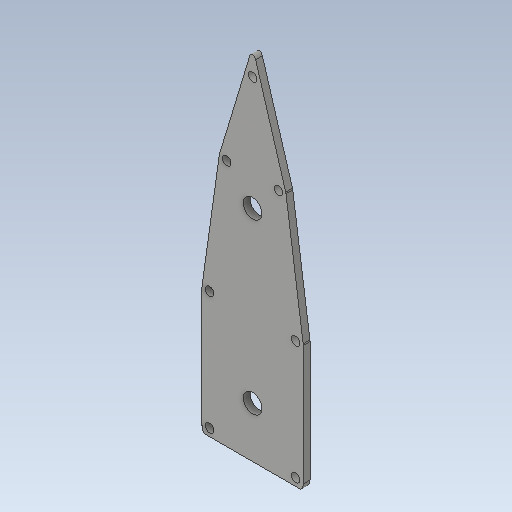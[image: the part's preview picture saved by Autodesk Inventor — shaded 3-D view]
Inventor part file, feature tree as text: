
AUTODESK INVENTOR PART (.ipt)
format: ipt  version: 2020.1 (Build 241239000, 239)  size: 233,984 bytes
history: native  units: mm
features: other x8, sketch x2, plane x1, sheet_metal_op x1, reference x1, projected_geometry x1
ambient origin geometry x8: Origin, YZ Plane, XZ Plane, XY Plane, X Axis, Y Axis, Z Axis, Center Point
bodies: Solid1 (feature_tree)
feature tree (14):
  plane  "Work Plane1"
  sheet_metal_op  "Face1"
  sketch  "Sketch1"  dims[d0=8.0mm]
  reference  "Reference1"
  other  "Plate1"
  sketch  "Sketch2"  dims[d1=22.0mm d2=22.0mm d3=10.0mm d4=10.0mm d5=10.0mm d6=10.0mm d7=10.0mm d8=10.0mm d9=10.0mm d10=10.0mm d11=10.0mm d12=10.0mm d13=10.0mm d14=10.0mm d15=9.0mm d16=9.0mm d17=4.0mm d18=9.0mm d19=9.0mm d20=9.0mm d21=9.0mm d22=9.0mm d23=9.0mm d24=9.0mm d25=9.0mm d26=9.0mm d27=9.0mm d28=9.0mm d29=9.0mm d30=60.0mm d31=60.0mm d33=200.0mm d34=8.0mm d35=0.0mm]
  projected_geometry  "Projected Loop1"
  other  "zinkdrænshuller"
  parser-record x2  (decoder bookkeeping rows leaked as tree rows — omitted from the tree; the rows remain in map.json)
  other  "modul bund.iam"
  other  "vange bund:1"
  other  "Definition1"
  other  "plade bund:1"
note: 2 file-system paths scrubbed to <path> (originals preserved in map.json)
